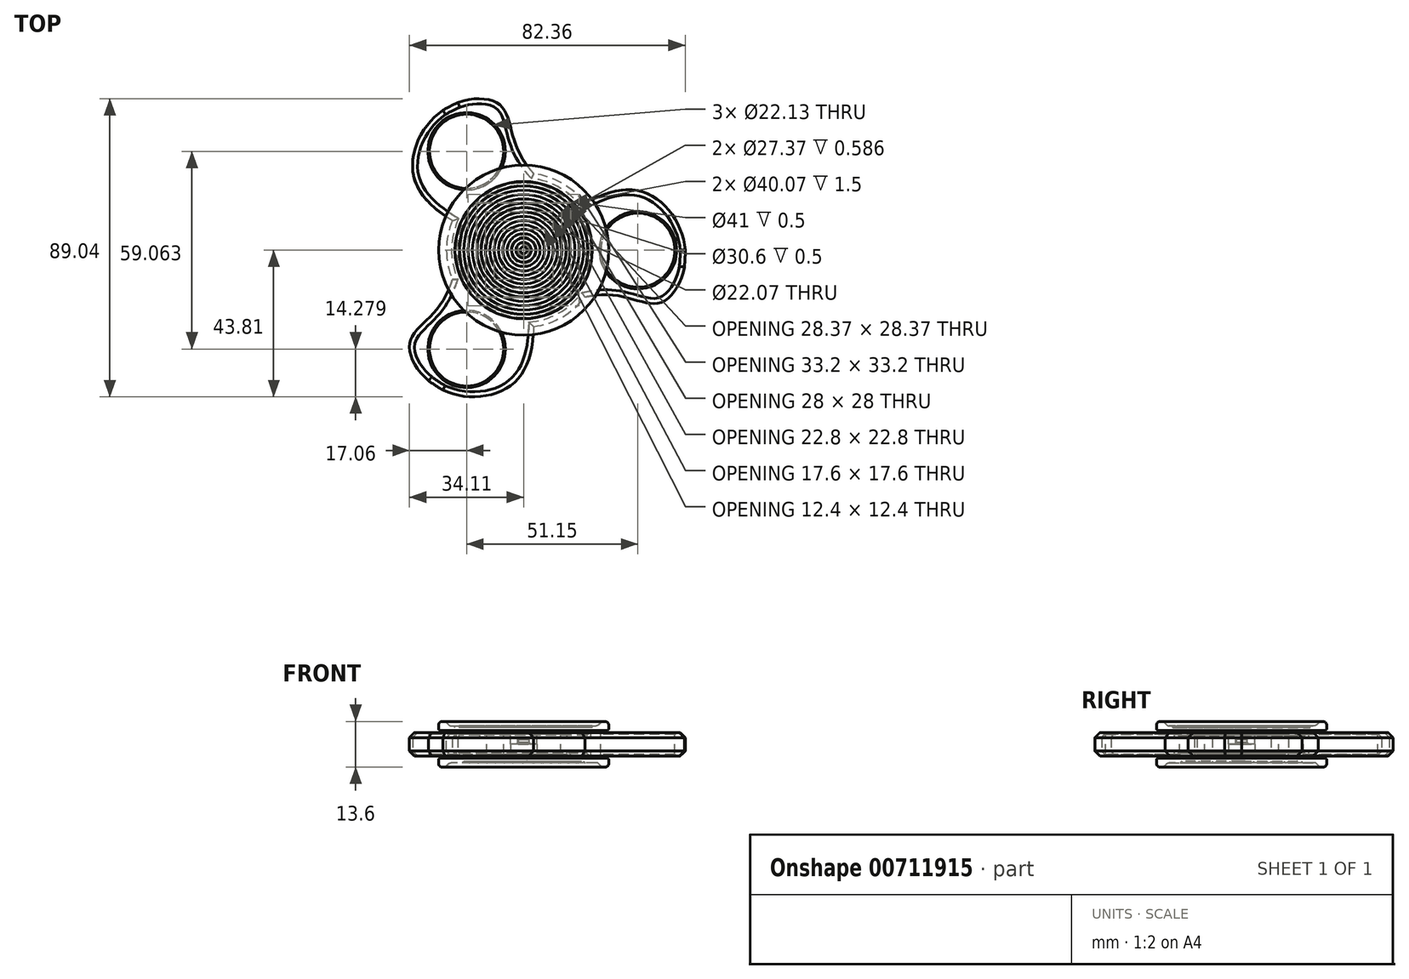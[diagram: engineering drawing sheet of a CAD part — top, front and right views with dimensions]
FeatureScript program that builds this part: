
annotation { "Feature Type Name" : "Feature", "Feature Type Description" : "" }
export const myFeature = defineFeature(function(context is Context, id is Id, definition is map)
    precondition{}
    {
        {
            var Q0;
            Q0=qCreatedBy(makeId("Front.planeOp"),FACE);
            var sketch = newSketch(context, id + "F0", { "sketchPlane" : qUnion([Q0])});
            skLineSegment(sketch, "E0", {"start": v(0, 0) * mm, "end": v(0, 3.5) * mm});
            skLineSegment(sketch, "E1", {"start": v(0, 3.5) * mm, "end": v(13.04, 3.5) * mm});
            skLineSegment(sketch, "E2", {"start": v(13.04, 3.5) * mm, "end": v(13.04, 2) * mm});
            skLineSegment(sketch, "E3", {"start": v(13.04, 2) * mm, "end": v(20.04, 2) * mm});
            skLineSegment(sketch, "E4", {"start": v(20.04, 2) * mm, "end": v(20.04, 3.5) * mm});
            skLineSegment(sketch, "E5", {"start": v(20.04, 3.5) * mm, "end": v(23.04, 3.5) * mm});
            skLineSegment(sketch, "E6", {"start": v(23.04, 3.5) * mm, "end": v(23.04, 0) * mm});
            skLineSegment(sketch, "E7", {"start": v(23.04, 0) * mm, "end": v(45.16, 0) * mm});
            skLineSegment(sketch, "E8", {"start": v(45.16, 0) * mm, "end": v(45.16, 3.5) * mm});
            skLineSegment(sketch, "E9", {"start": v(45.16, 3.5) * mm, "end": v(47.16, 3.5) * mm});
            skLineSegment(sketch, "E10", {"start": v(47.16, 3.5) * mm, "end": v(48.16, 1.5) * mm});
            skLineSegment(sketch, "E11", {"start": v(48.16, 1.5) * mm, "end": v(48.16, 0) * mm});
            skLineSegment(sketch, "E12", {"start": v(48.16, 0) * mm, "end": v(45.16, 0) * mm});
            skLineSegment(sketch, "E13", {"start": v(23.04, 0) * mm, "end": v(11.04, 0) * mm});
            skLineSegment(sketch, "E14", {"start": v(11.04, 0) * mm, "end": v(11.04, 3.5) * mm});
            skLineSegment(sketch, "E15", {"start": v(23.04, 3.5) * mm, "end": v(45.16, 3.5) * mm});
            skLineSegment(sketch, "E16", {"start": v(34.1, 0) * mm, "end": v(34.1, 3.5) * mm});
            skLineSegment(sketch, "E17", {"start": v(13.68, 4.15) * mm, "end": v(13.68, 2.65) * mm});
            skLineSegment(sketch, "E18", {"start": v(13.68, 2.65) * mm, "end": v(19.38, 2.65) * mm});
            skLineSegment(sketch, "E19", {"start": v(19.38, 2.65) * mm, "end": v(19.38, 4.15) * mm});
            skLineSegment(sketch, "E20", {"start": v(19.38, 4.15) * mm, "end": v(25.38, 4.15) * mm});
            skLineSegment(sketch, "E21", {"start": v(25.38, 4.15) * mm, "end": v(25.38, 5.5) * mm});
            skLineSegment(sketch, "E22", {"start": v(25.38, 5.5) * mm, "end": v(0, 5.5) * mm});
            skLineSegment(sketch, "E23", {"start": v(0, 5.5) * mm, "end": v(0, 0) * mm});
            skLineSegment(sketch, "E24", {"start": v(0, 0) * mm, "end": v(3.97, 0) * mm});
            skLineSegment(sketch, "E25", {"start": v(3.97, 0) * mm, "end": v(3.97, 3.5) * mm});
            skLineSegment(sketch, "E26", {"start": v(3.97, 3.5) * mm, "end": v(4.97, 3.5) * mm});
            skLineSegment(sketch, "E27", {"start": v(4.97, 3.5) * mm, "end": v(4.97, 4.15) * mm});
            skLineSegment(sketch, "E28", {"start": v(4.97, 4.15) * mm, "end": v(13.68, 4.15) * mm});
            skLineSegment(sketch, "E29", {"start": v(25.38, 5.5) * mm, "end": v(25.38, 6.8) * mm});
            skLineSegment(sketch, "E30", {"start": v(25.38, 6.8) * mm, "end": v(23.38, 6.8) * mm});
            skLineSegment(sketch, "E31", {"start": v(23.38, 6.8) * mm, "end": v(22.08, 5.5) * mm});
            skLineSegment(sketch, "E32.bottom", {"start": v(1, 5.5) * mm, "end": v(2.3, 5.5) * mm});
            skLineSegment(sketch, "E32.top", {"start": v(1, 5) * mm, "end": v(2.3, 5) * mm});
            skLineSegment(sketch, "E32.left", {"start": v(1, 5.5) * mm, "end": v(1, 5) * mm});
            skLineSegment(sketch, "E32.right", {"start": v(2.3, 5.5) * mm, "end": v(2.3, 5) * mm});
            skLineSegment(sketch, "E33.1.0.0", {"start": v(4.9, 5.5) * mm, "end": v(4.9, 5) * mm});
            skLineSegment(sketch, "E33.1.0.1", {"start": v(3.6, 5) * mm, "end": v(4.9, 5) * mm});
            skLineSegment(sketch, "E33.1.0.2", {"start": v(3.6, 5.5) * mm, "end": v(3.6, 5) * mm});
            skLineSegment(sketch, "E33.2.0.0", {"start": v(7.5, 5.5) * mm, "end": v(7.5, 5) * mm});
            skLineSegment(sketch, "E33.2.0.1", {"start": v(6.2, 5) * mm, "end": v(7.5, 5) * mm});
            skLineSegment(sketch, "E33.2.0.2", {"start": v(6.2, 5.5) * mm, "end": v(6.2, 5) * mm});
            skLineSegment(sketch, "E33.3.0.0", {"start": v(10.1, 5.5) * mm, "end": v(10.1, 5) * mm});
            skLineSegment(sketch, "E33.3.0.1", {"start": v(8.8, 5) * mm, "end": v(10.1, 5) * mm});
            skLineSegment(sketch, "E33.3.0.2", {"start": v(8.8, 5.5) * mm, "end": v(8.8, 5) * mm});
            skLineSegment(sketch, "E33.4.0.0", {"start": v(12.7, 5.5) * mm, "end": v(12.7, 5) * mm});
            skLineSegment(sketch, "E33.4.0.1", {"start": v(11.4, 5) * mm, "end": v(12.7, 5) * mm});
            skLineSegment(sketch, "E33.4.0.2", {"start": v(11.4, 5.5) * mm, "end": v(11.4, 5) * mm});
            skLineSegment(sketch, "E33.5.0.0", {"start": v(15.3, 5.5) * mm, "end": v(15.3, 5) * mm});
            skLineSegment(sketch, "E33.5.0.1", {"start": v(14, 5) * mm, "end": v(15.3, 5) * mm});
            skLineSegment(sketch, "E33.5.0.2", {"start": v(14, 5.5) * mm, "end": v(14, 5) * mm});
            skLineSegment(sketch, "E33.6.0.0", {"start": v(17.9, 5.5) * mm, "end": v(17.9, 5) * mm});
            skLineSegment(sketch, "E33.6.0.1", {"start": v(16.6, 5) * mm, "end": v(17.9, 5) * mm});
            skLineSegment(sketch, "E33.6.0.2", {"start": v(16.6, 5.5) * mm, "end": v(16.6, 5) * mm});
            skLineSegment(sketch, "E33.direction1", {"start": v(2.3, 5) * mm, "end": v(4.9, 5) * mm, "construction": true});
            skLineSegment(sketch, "E34.MirrorCS", {"start": v(2.3, -5.5) * mm, "end": v(2.3, -5) * mm});
            skLineSegment(sketch, "E35.MirrorCS", {"start": v(3.6, -5) * mm, "end": v(4.9, -5) * mm});
            skLineSegment(sketch, "E36.MirrorCS", {"start": v(1, -5.5) * mm, "end": v(2.3, -5.5) * mm});
            skLineSegment(sketch, "E37.MirrorCS", {"start": v(1, -5) * mm, "end": v(2.3, -5) * mm});
            skLineSegment(sketch, "E38.MirrorCS", {"start": v(4.9, -5.5) * mm, "end": v(4.9, -5) * mm});
            skLineSegment(sketch, "E39.MirrorCS", {"start": v(13.04, -3.5) * mm, "end": v(13.04, -2) * mm});
            skLineSegment(sketch, "E40.MirrorCS", {"start": v(6.2, -5.5) * mm, "end": v(6.2, -5) * mm});
            skLineSegment(sketch, "E41.MirrorCS", {"start": v(1, -5.5) * mm, "end": v(1, -5) * mm});
            skLineSegment(sketch, "E42.MirrorCS", {"start": v(3.6, -5.5) * mm, "end": v(3.6, -5) * mm});
            skLineSegment(sketch, "E43.MirrorCS", {"start": v(2.3, -5) * mm, "end": v(4.9, -5) * mm, "construction": true});
            skLineSegment(sketch, "E44.MirrorCS", {"start": v(10.1, -5.5) * mm, "end": v(10.1, -5) * mm});
            skLineSegment(sketch, "E45.MirrorCS", {"start": v(3.97, -3.5) * mm, "end": v(4.97, -3.5) * mm});
            skLineSegment(sketch, "E46.MirrorCS", {"start": v(19.38, -2.65) * mm, "end": v(19.38, -4.15) * mm});
            skLineSegment(sketch, "E47.MirrorCS", {"start": v(17.9, -5.5) * mm, "end": v(17.9, -5) * mm});
            skLineSegment(sketch, "E48.MirrorCS", {"start": v(8.8, -5) * mm, "end": v(10.1, -5) * mm});
            skLineSegment(sketch, "E49.MirrorCS", {"start": v(4.97, -3.5) * mm, "end": v(4.97, -4.15) * mm});
            skLineSegment(sketch, "E50.MirrorCS", {"start": v(19.38, -4.15) * mm, "end": v(25.38, -4.15) * mm});
            skLineSegment(sketch, "E51.MirrorCS", {"start": v(12.7, -5.5) * mm, "end": v(12.7, -5) * mm});
            skLineSegment(sketch, "E52.MirrorCS", {"start": v(16.6, -5) * mm, "end": v(17.9, -5) * mm});
            skLineSegment(sketch, "E53.MirrorCS", {"start": v(25.38, -5.5) * mm, "end": v(25.38, -6.8) * mm});
            skLineSegment(sketch, "E54.MirrorCS", {"start": v(8.8, -5.5) * mm, "end": v(8.8, -5) * mm});
            skLineSegment(sketch, "E55.MirrorCS", {"start": v(11.4, -5) * mm, "end": v(12.7, -5) * mm});
            skLineSegment(sketch, "E56.MirrorCS", {"start": v(16.6, -5.5) * mm, "end": v(16.6, -5) * mm});
            skLineSegment(sketch, "E57.MirrorCS", {"start": v(25.38, -6.8) * mm, "end": v(23.38, -6.8) * mm});
            skLineSegment(sketch, "E58.MirrorCS", {"start": v(14, -5.5) * mm, "end": v(14, -5) * mm});
            skLineSegment(sketch, "E59.MirrorCS", {"start": v(20.04, -3.5) * mm, "end": v(23.04, -3.5) * mm});
            skLineSegment(sketch, "E60.MirrorCS", {"start": v(20.04, -2) * mm, "end": v(20.04, -3.5) * mm});
            skLineSegment(sketch, "E61.MirrorCS", {"start": v(6.2, -5) * mm, "end": v(7.5, -5) * mm});
            skLineSegment(sketch, "E62.MirrorCS", {"start": v(15.3, -5.5) * mm, "end": v(15.3, -5) * mm});
            skLineSegment(sketch, "E63.MirrorCS", {"start": v(47.16, -3.5) * mm, "end": v(48.16, -1.5) * mm});
            skLineSegment(sketch, "E64.MirrorCS", {"start": v(45.16, -3.5) * mm, "end": v(47.16, -3.5) * mm});
            skLineSegment(sketch, "E65.MirrorCS", {"start": v(14, -5) * mm, "end": v(15.3, -5) * mm});
            skLineSegment(sketch, "E66.MirrorCS", {"start": v(7.5, -5.5) * mm, "end": v(7.5, -5) * mm});
            skLineSegment(sketch, "E67.MirrorCS", {"start": v(11.4, -5.5) * mm, "end": v(11.4, -5) * mm});
            skLineSegment(sketch, "E68.MirrorCS", {"start": v(13.69, -4.15) * mm, "end": v(13.69, -2.65) * mm});
            skLineSegment(sketch, "E69.MirrorCS", {"start": v(25.38, -4.15) * mm, "end": v(25.38, -5.5) * mm});
            skLineSegment(sketch, "E70.MirrorCS", {"start": v(23.38, -6.8) * mm, "end": v(22.08, -5.5) * mm});
            skLineSegment(sketch, "E71.MirrorCS", {"start": v(4.97, -4.15) * mm, "end": v(13.68, -4.15) * mm});
            skLineSegment(sketch, "E72.MirrorCS", {"start": v(0, -3.5) * mm, "end": v(13.04, -3.5) * mm});
            skLineSegment(sketch, "E73.MirrorCS", {"start": v(23.04, -3.5) * mm, "end": v(45.16, -3.5) * mm});
            skLineSegment(sketch, "E74.MirrorCS", {"start": v(13.04, -2) * mm, "end": v(20.04, -2) * mm});
            skLineSegment(sketch, "E75.MirrorCS", {"start": v(13.68, -2.65) * mm, "end": v(19.38, -2.65) * mm});
            skLineSegment(sketch, "E76.MirrorCS", {"start": v(25.38, -5.5) * mm, "end": v(0, -5.5) * mm});
            skLineSegment(sketch, "E77.MirrorCS", {"start": v(48.16, -1.5) * mm, "end": v(48.16, 0) * mm});
            skLineSegment(sketch, "E78.MirrorCS", {"start": v(45.16, 0) * mm, "end": v(45.16, -3.5) * mm});
            skLineSegment(sketch, "E79.MirrorCS", {"start": v(34.1, 0) * mm, "end": v(34.1, -3.5) * mm});
            skLineSegment(sketch, "E80.MirrorCS", {"start": v(23.04, -3.5) * mm, "end": v(23.04, 0) * mm});
            skLineSegment(sketch, "E81.MirrorCS", {"start": v(11.04, 0) * mm, "end": v(11.04, -3.5) * mm});
            skLineSegment(sketch, "E82.MirrorCS", {"start": v(3.97, 0) * mm, "end": v(3.97, -3.5) * mm});
            skLineSegment(sketch, "E83.MirrorCS", {"start": v(0, -5.5) * mm, "end": v(0, 0) * mm});
            skLineSegment(sketch, "E84", {"start": v(1.6, 0) * mm, "end": v(1.6, 2) * mm});
            skLineSegment(sketch, "E85", {"start": v(1.6, 2) * mm, "end": v(0, 2) * mm});
            skLineSegment(sketch, "E86.0", {"start": v(1.7, 2.1) * mm, "end": v(0, 2.1) * mm});
            skLineSegment(sketch, "E86.1", {"start": v(1.7, 0) * mm, "end": v(1.7, 2.1) * mm});
            skLineSegment(sketch, "E87.0.7.0", {"start": v(20.5, 5.5) * mm, "end": v(20.5, 5) * mm});
            skLineSegment(sketch, "E87.3.7.0", {"start": v(19.2, 5) * mm, "end": v(20.5, 5) * mm});
            skLineSegment(sketch, "E87.6.7.0", {"start": v(19.2, 5.5) * mm, "end": v(19.2, 5) * mm});
            skSolve(sketch);
        }
        {
            var Q0;
            {var subQ1=sQuery(id+"F0.wireOp",EDGE,"E2");Q0=makeQuery(id+"F0.imprint","IMPRINT",FACE,{"disambiguationData":[TD([[makeQuery(id+"F0.imprint","IMPRINT",EDGE,{"derivedFrom":subQ1}),-1.0]])]});}
            var Q1;
            Q1=makeQuery(id+"F0.imprint","IMPRINT",FACE,{"disambiguationData":[TD([[makeQuery(id+"F0.imprint","IMPRINT",EDGE,{"derivedFrom":sQuery(id+"F0.wireOp",EDGE,"E13")}),1.0]])]});
            var Q2;
            {var subQ0=sQuery(id+"F0.wireOp",EDGE,"E6");Q2=makeQuery(id+"F0.imprint","IMPRINT",FACE,{"disambiguationData":[TD([[makeQuery(id+"F0.imprint","IMPRINT",EDGE,{"derivedFrom":subQ0}),1.0]])]});}
            var Q3;
            {var subQ2=sQuery(id+"F0.wireOp",EDGE,"E79.MirrorCS");Q3=makeQuery(id+"F0.imprint","IMPRINT",FACE,{"disambiguationData":[TD([[makeQuery(id+"F0.imprint","IMPRINT",EDGE,{"derivedFrom":subQ2}),-1.0]])]});}
            var Q4;
            {var subQ0=sQuery(id+"F0.wireOp",EDGE,"E8");Q4=makeQuery(id+"F0.imprint","IMPRINT",FACE,{"disambiguationData":[TD([[makeQuery(id+"F0.imprint","IMPRINT",EDGE,{"derivedFrom":subQ0}),1.0]])]});}
            var Q5;
            {var subQ0=sQuery(id+"F0.wireOp",EDGE,"E78.MirrorCS");Q5=makeQuery(id+"F0.imprint","IMPRINT",FACE,{"disambiguationData":[TD([[makeQuery(id+"F0.imprint","IMPRINT",EDGE,{"derivedFrom":subQ0}),-1.0]])]});}
            var Q6;
            Q6=makeQuery(id+"F0.imprint","IMPRINT",FACE,{"disambiguationData":[TD([[makeQuery(id+"F0.imprint","IMPRINT",EDGE,{"derivedFrom":sQuery(id+"F0.wireOp",EDGE,"E8")}),-1.0]])]});
            var Q7;
            Q7=makeQuery(id+"F0.imprint","IMPRINT",FACE,{"disambiguationData":[TD([[makeQuery(id+"F0.imprint","IMPRINT",EDGE,{"derivedFrom":sQuery(id+"F0.wireOp",EDGE,"E12")}),1.0]])]});
            var Q8;
            Q8=sQuery(id+"F0.wireOp",EDGE,"E23");
            revolve(context, id + "F1", {"surfaceOperationType" : NewSurfaceOperationType.NEW, "entities" : qUnion([Q0, Q1, Q2, Q3, Q4, Q5, Q6, Q7]), "axis" : qUnion([Q8]), "revolveType" : RevolveType.FULL});
        }
        {
            var Q0;
            {var subQ0=sQuery(id+"F0.wireOp",EDGE,"E8");Q0=makeQuery(id+"F0.imprint","IMPRINT",FACE,{"disambiguationData":[TD([[makeQuery(id+"F0.imprint","IMPRINT",EDGE,{"derivedFrom":subQ0}),1.0]])]});}
            var Q1;
            {var subQ0=sQuery(id+"F0.wireOp",EDGE,"E78.MirrorCS");Q1=makeQuery(id+"F0.imprint","IMPRINT",FACE,{"disambiguationData":[TD([[makeQuery(id+"F0.imprint","IMPRINT",EDGE,{"derivedFrom":subQ0}),-1.0]])]});}
            var Q2;
            Q2=sQuery(id+"F0.wireOp",EDGE,"E79.MirrorCS");
            revolve(context, id + "F2", {"surfaceOperationType" : NewSurfaceOperationType.NEW, "entities" : qUnion([Q0, Q1]), "axis" : qUnion([Q2]), "revolveType" : RevolveType.FULL});
        }
        {
            var Q0;
            Q0=makeQuery(id+"F0.imprint","IMPRINT",FACE,{"disambiguationData":[TD([[makeQuery(id+"F0.imprint","IMPRINT",EDGE,{"derivedFrom":sQuery(id+"F0.wireOp",EDGE,"E17")}),1.0]])]});
            var Q1;
            {var subQ0=sQuery(id+"F0.wireOp",EDGE,"E29");Q1=makeQuery(id+"F0.imprint","IMPRINT",FACE,{"disambiguationData":[TD([[makeQuery(id+"F0.imprint","IMPRINT",EDGE,{"derivedFrom":subQ0}),1.0]])]});}
            var Q2;
            {var subQ0=sQuery(id+"F0.wireOp",EDGE,"E25");Q2=makeQuery(id+"F0.imprint","IMPRINT",FACE,{"disambiguationData":[TD([[makeQuery(id+"F0.imprint","IMPRINT",EDGE,{"derivedFrom":subQ0}),1.0]])]});}
            var Q3;
            Q3=sQuery(id+"F0.wireOp",EDGE,"E23");
            revolve(context, id + "F3", {"surfaceOperationType" : NewSurfaceOperationType.NEW, "entities" : qUnion([Q0, Q1, Q2]), "axis" : qUnion([Q3]), "revolveType" : RevolveType.FULL});
        }
        {
            var Q0;
            {var subQ15=sQuery(id+"F0.wireOp",EDGE,"E34.MirrorCS");Q0=makeQuery(id+"F0.imprint","IMPRINT",FACE,{"disambiguationData":[TD([[makeQuery(id+"F0.imprint","IMPRINT",EDGE,{"derivedFrom":subQ15}),-1.0]])]});}
            var Q1;
            {var subQ3=sQuery(id+"F0.wireOp",EDGE,"E82.MirrorCS");Q1=makeQuery(id+"F0.imprint","IMPRINT",FACE,{"disambiguationData":[TD([[makeQuery(id+"F0.imprint","IMPRINT",EDGE,{"derivedFrom":subQ3}),-1.0]])]});}
            var Q2;
            {var subQ4=sQuery(id+"F0.wireOp",EDGE,"E84");Q2=makeQuery(id+"F0.imprint","IMPRINT",FACE,{"disambiguationData":[TD([[makeQuery(id+"F0.imprint","IMPRINT",EDGE,{"derivedFrom":subQ4}),1.0]])]});}
            var Q3;
            {var subQ0=sQuery(id+"F0.wireOp",EDGE,"E53.MirrorCS");Q3=makeQuery(id+"F0.imprint","IMPRINT",FACE,{"disambiguationData":[TD([[makeQuery(id+"F0.imprint","IMPRINT",EDGE,{"derivedFrom":subQ0}),-1.0]])]});}
            var Q4;
            Q4=sQuery(id+"F0.wireOp",EDGE,"E83.MirrorCS");
            revolve(context, id + "F4", {"surfaceOperationType" : NewSurfaceOperationType.NEW, "entities" : qUnion([Q0, Q1, Q2, Q3]), "axis" : qUnion([Q4]), "revolveType" : RevolveType.FULL});
        }
        {
            var Q0;
            Q0=makeQuery(id+"F2.opRevolve","SWEPT_BODY",BODY,{"disambiguationData":[OSD([sQuery(id+"F0.wireOp",EDGE,"E8"),sQuery(id+"F0.wireOp",EDGE,"E15"),sQuery(id+"F0.wireOp",EDGE,"E16"),sQuery(id+"F0.wireOp",EDGE,"E73.MirrorCS"),sQuery(id+"F0.wireOp",EDGE,"E78.MirrorCS"),sQuery(id+"F0.wireOp",EDGE,"E79.MirrorCS")])]});
            var Q1;
            Q1=makeQuery(id+"F1.opRevolve","SWEPT_EDGE",EDGE,{"disambiguationData":[OSD([sQuery(id+"F0.wireOp",EDGE,"E72.MirrorCS"),sQuery(id+"F0.wireOp",EDGE,"E81.MirrorCS")])]});
            circularPattern(context, id + "F5", {"entities" : qUnion([Q0]), "axis" : qUnion([Q1]), "angle" : 360 * degree, "instanceCount" : 3, "equalSpace" : true});
        }
        {
            var Q0;
            Q0=qCreatedBy(makeId("Top.planeOp"),FACE);
            var sketch = newSketch(context, id + "F6", { "sketchPlane" : qUnion([Q0])});
            skCircle(sketch, "E88", {"center": v(0, 0) * mm, "radius": 48.25 * mm});
            skFitSpline(sketch, "E89", {"points": [v(0, -25) * mm, v(27.25, -13.5) * mm, v(41.25, -15.5) * mm, v(48.25, 0) * mm, v(34, 17.78) * mm, v(0, 0) * mm], "startDerivative": vector(107.2, 120.6) * mm, "endDerivative": vector(-125.88, -120.18) * mm});
            skCircle(sketch, "E90", {"center": v(0, 0) * mm, "radius": 22.05 * mm});
            skSolve(sketch);
        }
        {
            var Q0;
            {var subQ0=sQuery(id+"F6.wireOp",EDGE,"E89");var subQ1=sQuery(id+"F6.wireOp",EDGE,"E88");var subQ2=makeQuery(id+"F6.imprint","INTERSECT",VERTEX,{"disambiguationData":[OD(0.0)],"derivedFrom":[subQ1,subQ0]});Q0=makeQuery(id+"F6.imprint","IMPRINT",FACE,{"disambiguationData":[TD([[makeQuery(id+"F6.imprint","IMPRINT",EDGE,{"disambiguationData":[TD([[subQ2,-1.0]])],"derivedFrom":subQ1}),1.0]])]});}
            extrude(context, id + "F7", {"entities" : qUnion([Q0]), "depth" : 3.5 * mm, "offsetDistance" : 25 * mm, "hasSecondDirection" : true, "secondDirectionOppositeDirection" : true, "secondDirectionDepth" : 3.5 * mm});
        }
        {
            var Q0;
            Q0=makeQuery(id+"F7.opExtrude","SWEPT_BODY",BODY,{"disambiguationData":[OSD([sQuery(id+"F6.wireOp",EDGE,"E88"),sQuery(id+"F6.wireOp",EDGE,"E89"),sQuery(id+"F6.wireOp",EDGE,"E90")])]});
            var Q1;
            Q1=makeQuery(id+"F1.opRevolve","SWEPT_FACE",FACE,{"disambiguationData":[OSD([sQuery(id+"F0.wireOp",EDGE,"E14"),sQuery(id+"F0.wireOp",EDGE,"E81.MirrorCS")])]});
            circularPattern(context, id + "F8", {"entities" : qUnion([Q0]), "axis" : qUnion([Q1]), "angle" : 360 * degree, "instanceCount" : 3, "equalSpace" : true});
        }
        {
            var Q0;
            {var subQ1=sQuery(id+"F0.wireOp",EDGE,"E2");Q0=makeQuery(id+"F0.imprint","IMPRINT",FACE,{"disambiguationData":[TD([[makeQuery(id+"F0.imprint","IMPRINT",EDGE,{"derivedFrom":subQ1}),-1.0]])]});}
            var Q1;
            Q1=makeQuery(id+"F0.imprint","IMPRINT",FACE,{"disambiguationData":[TD([[makeQuery(id+"F0.imprint","IMPRINT",EDGE,{"derivedFrom":sQuery(id+"F0.wireOp",EDGE,"E13")}),1.0]])]});
            var Q2;
            Q2=sQuery(id+"F0.wireOp",EDGE,"E23");
            revolve(context, id + "F9", {"surfaceOperationType" : NewSurfaceOperationType.NEW, "entities" : qUnion([Q0, Q1]), "axis" : qUnion([Q2]), "revolveType" : RevolveType.FULL});
        }
        {
            var Q0;
            Q0=makeQuery(id+"F8.opPattern","COPY",BODY,{"derivedFrom":makeQuery(id+"F7.opExtrude","SWEPT_BODY",BODY,{"disambiguationData":[OSD([sQuery(id+"F6.wireOp",EDGE,"E88"),sQuery(id+"F6.wireOp",EDGE,"E89"),sQuery(id+"F6.wireOp",EDGE,"E90")])]}),"instanceName":"2"});
            var Q1;
            Q1=makeQuery(id+"F8.opPattern","COPY",BODY,{"derivedFrom":makeQuery(id+"F7.opExtrude","SWEPT_BODY",BODY,{"disambiguationData":[OSD([sQuery(id+"F6.wireOp",EDGE,"E88"),sQuery(id+"F6.wireOp",EDGE,"E89"),sQuery(id+"F6.wireOp",EDGE,"E90")])]}),"instanceName":"1"});
            var Q2;
            Q2=makeQuery(id+"F7.opExtrude","SWEPT_BODY",BODY,{"disambiguationData":[OSD([sQuery(id+"F6.wireOp",EDGE,"E88"),sQuery(id+"F6.wireOp",EDGE,"E89"),sQuery(id+"F6.wireOp",EDGE,"E90")])]});
            var Q3;
            Q3=makeQuery(id+"F9.opRevolve","SWEPT_BODY",BODY,{"disambiguationData":[OSD([sQuery(id+"F0.wireOp",EDGE,"E1"),sQuery(id+"F0.wireOp",EDGE,"E2"),sQuery(id+"F0.wireOp",EDGE,"E3"),sQuery(id+"F0.wireOp",EDGE,"E4"),sQuery(id+"F0.wireOp",EDGE,"E5"),sQuery(id+"F0.wireOp",EDGE,"E6"),sQuery(id+"F0.wireOp",EDGE,"E23"),sQuery(id+"F0.wireOp",EDGE,"E26"),sQuery(id+"F0.wireOp",EDGE,"E39.MirrorCS"),sQuery(id+"F0.wireOp",EDGE,"E59.MirrorCS"),sQuery(id+"F0.wireOp",EDGE,"E60.MirrorCS"),sQuery(id+"F0.wireOp",EDGE,"E72.MirrorCS"),sQuery(id+"F0.wireOp",EDGE,"E74.MirrorCS"),sQuery(id+"F0.wireOp",EDGE,"E80.MirrorCS"),sQuery(id+"F0.wireOp",EDGE,"E83.MirrorCS")])]});
            booleanBodies(context, id + "F10", {"operationType" : BooleanOperationType.UNION, "tools" : qUnion([Q0, Q1, Q2, Q3])});
        }
        {
            var Q0;
            Q0=makeQuery(id+"F1.opRevolve","SWEPT_BODY",BODY,{"disambiguationData":[OSD([sQuery(id+"F0.wireOp",EDGE,"E1"),sQuery(id+"F0.wireOp",EDGE,"E2"),sQuery(id+"F0.wireOp",EDGE,"E3"),sQuery(id+"F0.wireOp",EDGE,"E4"),sQuery(id+"F0.wireOp",EDGE,"E5"),sQuery(id+"F0.wireOp",EDGE,"E9"),sQuery(id+"F0.wireOp",EDGE,"E10"),sQuery(id+"F0.wireOp",EDGE,"E11"),sQuery(id+"F0.wireOp",EDGE,"E14"),sQuery(id+"F0.wireOp",EDGE,"E15"),sQuery(id+"F0.wireOp",EDGE,"E39.MirrorCS"),sQuery(id+"F0.wireOp",EDGE,"E59.MirrorCS"),sQuery(id+"F0.wireOp",EDGE,"E60.MirrorCS"),sQuery(id+"F0.wireOp",EDGE,"E63.MirrorCS"),sQuery(id+"F0.wireOp",EDGE,"E64.MirrorCS"),sQuery(id+"F0.wireOp",EDGE,"E72.MirrorCS"),sQuery(id+"F0.wireOp",EDGE,"E73.MirrorCS"),sQuery(id+"F0.wireOp",EDGE,"E74.MirrorCS"),sQuery(id+"F0.wireOp",EDGE,"E77.MirrorCS"),sQuery(id+"F0.wireOp",EDGE,"E81.MirrorCS")])]});
            deleteBodies(context, id + "F11", {"entities" : qUnion([Q0])});
        }
        {
            var Q0;
            Q0=makeQuery(id+"F5.opPattern","COPY",BODY,{"derivedFrom":makeQuery(id+"F2.opRevolve","SWEPT_BODY",BODY,{"disambiguationData":[OSD([sQuery(id+"F0.wireOp",EDGE,"E8"),sQuery(id+"F0.wireOp",EDGE,"E15"),sQuery(id+"F0.wireOp",EDGE,"E16"),sQuery(id+"F0.wireOp",EDGE,"E73.MirrorCS"),sQuery(id+"F0.wireOp",EDGE,"E78.MirrorCS"),sQuery(id+"F0.wireOp",EDGE,"E79.MirrorCS")])]}),"instanceName":"2"});
            var Q1;
            Q1=makeQuery(id+"F5.opPattern","COPY",BODY,{"derivedFrom":makeQuery(id+"F2.opRevolve","SWEPT_BODY",BODY,{"disambiguationData":[OSD([sQuery(id+"F0.wireOp",EDGE,"E8"),sQuery(id+"F0.wireOp",EDGE,"E15"),sQuery(id+"F0.wireOp",EDGE,"E16"),sQuery(id+"F0.wireOp",EDGE,"E73.MirrorCS"),sQuery(id+"F0.wireOp",EDGE,"E78.MirrorCS"),sQuery(id+"F0.wireOp",EDGE,"E79.MirrorCS")])]}),"instanceName":"1"});
            var Q2;
            Q2=makeQuery(id+"F2.opRevolve","SWEPT_BODY",BODY,{"disambiguationData":[OSD([sQuery(id+"F0.wireOp",EDGE,"E8"),sQuery(id+"F0.wireOp",EDGE,"E15"),sQuery(id+"F0.wireOp",EDGE,"E16"),sQuery(id+"F0.wireOp",EDGE,"E73.MirrorCS"),sQuery(id+"F0.wireOp",EDGE,"E78.MirrorCS"),sQuery(id+"F0.wireOp",EDGE,"E79.MirrorCS")])]});
            var Q3;
            Q3=makeQuery(id+"F8.opPattern","COPY",BODY,{"derivedFrom":makeQuery(id+"F7.opExtrude","SWEPT_BODY",BODY,{"disambiguationData":[OSD([sQuery(id+"F6.wireOp",EDGE,"E88"),sQuery(id+"F6.wireOp",EDGE,"E89"),sQuery(id+"F6.wireOp",EDGE,"E90")])]}),"instanceName":"2"});
            booleanBodies(context, id + "F12", {"operationType" : BooleanOperationType.SUBTRACTION, "tools" : qUnion([Q0, Q1, Q2]), "targets" : qUnion([Q3])});
        }
        {
            var Q0;
            Q0=makeQuery(id+"F9.opRevolve","SWEPT_EDGE",EDGE,{"disambiguationData":[OSD([sQuery(id+"F0.wireOp",EDGE,"E39.MirrorCS"),sQuery(id+"F0.wireOp",EDGE,"E72.MirrorCS")])]});
            var Q1;
            Q1=makeQuery(id+"F9.opRevolve","SWEPT_EDGE",EDGE,{"disambiguationData":[OSD([sQuery(id+"F0.wireOp",EDGE,"E72.MirrorCS"),sQuery(id+"F0.wireOp",EDGE,"E81.MirrorCS")])]});
            var Q2;
            Q2=makeQuery(id+"F12.opBoolean","COPY",FACE,{"derivedFrom":makeQuery(id+"F5.opPattern","COPY",FACE,{"derivedFrom":makeQuery(id+"F2.opRevolve","SWEPT_FACE",FACE,{"disambiguationData":[OSD([sQuery(id+"F0.wireOp",EDGE,"E8"),sQuery(id+"F0.wireOp",EDGE,"E78.MirrorCS")])]}),"instanceName":"1"})});
            var Q3;
            Q3=makeQuery(id+"F12.opBoolean","COPY",FACE,{"derivedFrom":makeQuery(id+"F5.opPattern","COPY",FACE,{"derivedFrom":makeQuery(id+"F2.opRevolve","SWEPT_FACE",FACE,{"disambiguationData":[OSD([sQuery(id+"F0.wireOp",EDGE,"E8"),sQuery(id+"F0.wireOp",EDGE,"E78.MirrorCS")])]}),"instanceName":"2"})});
            var Q4;
            Q4=makeQuery(id+"F12.opBoolean","COPY",FACE,{"derivedFrom":makeQuery(id+"F2.opRevolve","SWEPT_FACE",FACE,{"disambiguationData":[OSD([sQuery(id+"F0.wireOp",EDGE,"E8"),sQuery(id+"F0.wireOp",EDGE,"E78.MirrorCS")])]})});
            var Q5;
            Q5=makeQuery(id+"F9.opRevolve","SWEPT_FACE",FACE,{"disambiguationData":[OSD([sQuery(id+"F0.wireOp",EDGE,"E1")])]});
            var Q6;
            Q6=makeQuery(id+"F4.opRevolve","SWEPT_EDGE",EDGE,{"disambiguationData":[OSD([sQuery(id+"F0.wireOp",EDGE,"E84"),sQuery(id+"F0.wireOp",EDGE,"E85")])]});
            var Q7;
            Q7=makeQuery(id+"F4.opRevolve","SWEPT_EDGE",EDGE,{"disambiguationData":[OSD([sQuery(id+"F0.wireOp",EDGE,"E68.MirrorCS"),sQuery(id+"F0.wireOp",EDGE,"E75.MirrorCS")])]});
            var Q8;
            Q8=makeQuery(id+"F4.opRevolve","SWEPT_EDGE",EDGE,{"disambiguationData":[OSD([sQuery(id+"F0.wireOp",EDGE,"E46.MirrorCS"),sQuery(id+"F0.wireOp",EDGE,"E75.MirrorCS")])]});
            var Q9;
            Q9=makeQuery(id+"F3.opRevolve","SWEPT_EDGE",EDGE,{"disambiguationData":[OSD([sQuery(id+"F0.wireOp",EDGE,"E24"),sQuery(id+"F0.wireOp",EDGE,"E86.1")])]});
            var Q10;
            Q10=makeQuery(id+"F3.opRevolve","SWEPT_EDGE",EDGE,{"disambiguationData":[OSD([sQuery(id+"F0.wireOp",EDGE,"E17"),sQuery(id+"F0.wireOp",EDGE,"E18")])]});
            var Q11;
            Q11=makeQuery(id+"F3.opRevolve","SWEPT_EDGE",EDGE,{"disambiguationData":[OSD([sQuery(id+"F0.wireOp",EDGE,"E18"),sQuery(id+"F0.wireOp",EDGE,"E19")])]});
            chamfer(context, id + "F13", {"entities" : qUnion([Q0, Q1, Q2, Q3, Q4, Q5, Q6, Q7, Q8, Q9, Q10, Q11]), "width" : 0.5 * mm, "tangentPropagation" : true});
        }
        {
            var Q0;
            Q0=makeQuery(id+"F3.opRevolve","SWEPT_EDGE",EDGE,{"disambiguationData":[OSD([sQuery(id+"F0.wireOp",EDGE,"E30"),sQuery(id+"F0.wireOp",EDGE,"E31")])]});
            var Q1;
            Q1=makeQuery(id+"F3.opRevolve","SWEPT_EDGE",EDGE,{"disambiguationData":[OSD([sQuery(id+"F0.wireOp",EDGE,"E29"),sQuery(id+"F0.wireOp",EDGE,"E30")])]});
            var Q2;
            Q2=makeQuery(id+"F4.opRevolve","SWEPT_EDGE",EDGE,{"disambiguationData":[OSD([sQuery(id+"F0.wireOp",EDGE,"E53.MirrorCS"),sQuery(id+"F0.wireOp",EDGE,"E57.MirrorCS")])]});
            var Q3;
            Q3=makeQuery(id+"F4.opRevolve","SWEPT_EDGE",EDGE,{"disambiguationData":[OSD([sQuery(id+"F0.wireOp",EDGE,"E57.MirrorCS"),sQuery(id+"F0.wireOp",EDGE,"E70.MirrorCS")])]});
            var Q4;
            Q4=makeQuery(id+"F4.opRevolve","SWEPT_EDGE",EDGE,{"disambiguationData":[OSD([sQuery(id+"F0.wireOp",EDGE,"E41.MirrorCS"),sQuery(id+"F0.wireOp",EDGE,"E76.MirrorCS")])]});
            var Q5;
            Q5=makeQuery(id+"F3.opRevolve","SWEPT_EDGE",EDGE,{"disambiguationData":[OSD([sQuery(id+"F0.wireOp",EDGE,"E22"),sQuery(id+"F0.wireOp",EDGE,"E32.bottom"),sQuery(id+"F0.wireOp",EDGE,"E32.left")])]});
            var Q6;
            Q6=makeQuery(id+"F3.opRevolve","SWEPT_EDGE",EDGE,{"disambiguationData":[OSD([sQuery(id+"F0.wireOp",EDGE,"E22"),sQuery(id+"F0.wireOp",EDGE,"E31")])]});
            var Q7;
            Q7=makeQuery(id+"F4.opRevolve","SWEPT_EDGE",EDGE,{"disambiguationData":[OSD([sQuery(id+"F0.wireOp",EDGE,"E70.MirrorCS"),sQuery(id+"F0.wireOp",EDGE,"E76.MirrorCS")])]});
            var Q8;
            {var subQ0=sQuery(id+"F0.wireOp",EDGE,"E19");Q8=makeQuery(id+"F13.opChamfer","BLEND_EDGE",EDGE,{"blendedFrom":[makeQuery(id+"F3.opRevolve","SWEPT_EDGE",EDGE,{"disambiguationData":[OSD([sQuery(id+"F0.wireOp",EDGE,"E18"),subQ0])]}),makeQuery(id+"F3.opRevolve","SWEPT_FACE",FACE,{"disambiguationData":[OSD([subQ0])]})],"blendedInto":[makeQuery(id+"F3.opRevolve","SWEPT_FACE",FACE,{"disambiguationData":[OSD([subQ0])]})]});}
            var Q9;
            {var subQ0=sQuery(id+"F0.wireOp",EDGE,"E17");Q9=makeQuery(id+"F13.opChamfer","BLEND_EDGE",EDGE,{"blendedFrom":[makeQuery(id+"F3.opRevolve","SWEPT_EDGE",EDGE,{"disambiguationData":[OSD([subQ0,sQuery(id+"F0.wireOp",EDGE,"E18")])]}),makeQuery(id+"F3.opRevolve","SWEPT_FACE",FACE,{"disambiguationData":[OSD([subQ0])]})],"blendedInto":[makeQuery(id+"F3.opRevolve","SWEPT_FACE",FACE,{"disambiguationData":[OSD([subQ0])]})]});}
            var Q10;
            {var subQ0=sQuery(id+"F0.wireOp",EDGE,"E68.MirrorCS");Q10=makeQuery(id+"F13.opChamfer","BLEND_EDGE",EDGE,{"blendedFrom":[makeQuery(id+"F4.opRevolve","SWEPT_EDGE",EDGE,{"disambiguationData":[OSD([subQ0,sQuery(id+"F0.wireOp",EDGE,"E75.MirrorCS")])]}),makeQuery(id+"F4.opRevolve","SWEPT_FACE",FACE,{"disambiguationData":[OSD([subQ0])]})],"blendedInto":[makeQuery(id+"F4.opRevolve","SWEPT_FACE",FACE,{"disambiguationData":[OSD([subQ0])]})]});}
            var Q11;
            {var subQ0=sQuery(id+"F0.wireOp",EDGE,"E46.MirrorCS");Q11=makeQuery(id+"F13.opChamfer","BLEND_EDGE",EDGE,{"blendedFrom":[makeQuery(id+"F4.opRevolve","SWEPT_EDGE",EDGE,{"disambiguationData":[OSD([subQ0,sQuery(id+"F0.wireOp",EDGE,"E75.MirrorCS")])]}),makeQuery(id+"F4.opRevolve","SWEPT_FACE",FACE,{"disambiguationData":[OSD([subQ0])]})],"blendedInto":[makeQuery(id+"F4.opRevolve","SWEPT_FACE",FACE,{"disambiguationData":[OSD([subQ0])]})]});}
            fillet(context, id + "F14", {"entities" : qUnion([Q0, Q1, Q2, Q3, Q4, Q5, Q6, Q7, Q8, Q9, Q10, Q11]), "radius" : 1 * mm, "tangentPropagation" : true, "allowEdgeOverflow" : false});
        }
        {
            var Q0;
            {var subQ0=sQuery(id+"F0.wireOp",EDGE,"E22");Q0=makeQuery(id+"F3.opRevolve","SWEPT_FACE",FACE,{"disambiguationData":[OSD([subQ0]),TDD([makeQuery(id+"F0.imprint","IMPRINT",EDGE,{"disambiguationData":[TD([[makeQuery(id+"F0.imprint","INTERSECT",VERTEX,{"derivedFrom":[subQ0,sQuery(id+"F0.wireOp",EDGE,"E33.1.0.2")]}),-1.0]])],"derivedFrom":subQ0})])]});}
            var Q1;
            {var subQ0=sQuery(id+"F0.wireOp",EDGE,"E22");Q1=makeQuery(id+"F3.opRevolve","SWEPT_FACE",FACE,{"disambiguationData":[OSD([subQ0]),TDD([makeQuery(id+"F0.imprint","IMPRINT",EDGE,{"disambiguationData":[TD([[makeQuery(id+"F0.imprint","INTERSECT",VERTEX,{"derivedFrom":[subQ0,sQuery(id+"F0.wireOp",EDGE,"E33.1.0.0")]}),1.0]])],"derivedFrom":subQ0})])]});}
            var Q2;
            {var subQ0=sQuery(id+"F0.wireOp",EDGE,"E22");Q2=makeQuery(id+"F3.opRevolve","SWEPT_FACE",FACE,{"disambiguationData":[OSD([subQ0]),TDD([makeQuery(id+"F0.imprint","IMPRINT",EDGE,{"disambiguationData":[TD([[makeQuery(id+"F0.imprint","INTERSECT",VERTEX,{"derivedFrom":[subQ0,sQuery(id+"F0.wireOp",EDGE,"E33.2.0.0")]}),1.0]])],"derivedFrom":subQ0})])]});}
            var Q3;
            {var subQ0=sQuery(id+"F0.wireOp",EDGE,"E22");Q3=makeQuery(id+"F3.opRevolve","SWEPT_FACE",FACE,{"disambiguationData":[OSD([subQ0]),TDD([makeQuery(id+"F0.imprint","IMPRINT",EDGE,{"disambiguationData":[TD([[makeQuery(id+"F0.imprint","INTERSECT",VERTEX,{"derivedFrom":[subQ0,sQuery(id+"F0.wireOp",EDGE,"E33.3.0.0")]}),1.0]])],"derivedFrom":subQ0})])]});}
            var Q4;
            {var subQ0=sQuery(id+"F0.wireOp",EDGE,"E22");Q4=makeQuery(id+"F3.opRevolve","SWEPT_FACE",FACE,{"disambiguationData":[OSD([subQ0]),TDD([makeQuery(id+"F0.imprint","IMPRINT",EDGE,{"disambiguationData":[TD([[makeQuery(id+"F0.imprint","INTERSECT",VERTEX,{"derivedFrom":[subQ0,sQuery(id+"F0.wireOp",EDGE,"E33.4.0.0")]}),1.0]])],"derivedFrom":subQ0})])]});}
            var Q5;
            Q5=makeQuery(id+"F3.opRevolve","SWEPT_EDGE",EDGE,{"disambiguationData":[OSD([sQuery(id+"F0.wireOp",EDGE,"E22"),sQuery(id+"F0.wireOp",EDGE,"E33.6.0.2")])]});
            var Q6;
            Q6=makeQuery(id+"F3.opRevolve","SWEPT_EDGE",EDGE,{"disambiguationData":[OSD([sQuery(id+"F0.wireOp",EDGE,"E22"),sQuery(id+"F0.wireOp",EDGE,"E33.6.0.0")])]});
            var Q7;
            {var subQ0=sQuery(id+"F0.wireOp",EDGE,"E76.MirrorCS");Q7=makeQuery(id+"F4.opRevolve","SWEPT_FACE",FACE,{"disambiguationData":[OSD([subQ0]),TDD([makeQuery(id+"F0.imprint","IMPRINT",EDGE,{"disambiguationData":[TD([[makeQuery(id+"F0.imprint","INTERSECT",VERTEX,{"derivedFrom":[sQuery(id+"F0.wireOp",EDGE,"E34.MirrorCS"),subQ0]}),1.0]])],"derivedFrom":subQ0})])]});}
            var Q8;
            {var subQ0=sQuery(id+"F0.wireOp",EDGE,"E76.MirrorCS");Q8=makeQuery(id+"F4.opRevolve","SWEPT_FACE",FACE,{"disambiguationData":[OSD([subQ0]),TDD([makeQuery(id+"F0.imprint","IMPRINT",EDGE,{"disambiguationData":[TD([[makeQuery(id+"F0.imprint","INTERSECT",VERTEX,{"derivedFrom":[sQuery(id+"F0.wireOp",EDGE,"E38.MirrorCS"),subQ0]}),1.0]])],"derivedFrom":subQ0})])]});}
            var Q9;
            Q9=makeQuery(id+"F4.opRevolve","SWEPT_EDGE",EDGE,{"disambiguationData":[OSD([sQuery(id+"F0.wireOp",EDGE,"E54.MirrorCS"),sQuery(id+"F0.wireOp",EDGE,"E76.MirrorCS")])]});
            var Q10;
            {var subQ0=sQuery(id+"F0.wireOp",EDGE,"E76.MirrorCS");Q10=makeQuery(id+"F4.opRevolve","SWEPT_FACE",FACE,{"disambiguationData":[OSD([subQ0]),TDD([makeQuery(id+"F0.imprint","IMPRINT",EDGE,{"disambiguationData":[TD([[makeQuery(id+"F0.imprint","INTERSECT",VERTEX,{"derivedFrom":[sQuery(id+"F0.wireOp",EDGE,"E56.MirrorCS"),subQ0]}),-1.0]])],"derivedFrom":subQ0})])]});}
            var Q11;
            {var subQ0=sQuery(id+"F0.wireOp",EDGE,"E76.MirrorCS");Q11=makeQuery(id+"F4.opRevolve","SWEPT_FACE",FACE,{"disambiguationData":[OSD([subQ0]),TDD([makeQuery(id+"F0.imprint","IMPRINT",EDGE,{"disambiguationData":[TD([[makeQuery(id+"F0.imprint","INTERSECT",VERTEX,{"derivedFrom":[sQuery(id+"F0.wireOp",EDGE,"E51.MirrorCS"),subQ0]}),1.0]])],"derivedFrom":subQ0})])]});}
            var Q12;
            {var subQ0=sQuery(id+"F0.wireOp",EDGE,"E76.MirrorCS");Q12=makeQuery(id+"F4.opRevolve","SWEPT_FACE",FACE,{"disambiguationData":[OSD([subQ0]),TDD([makeQuery(id+"F0.imprint","IMPRINT",EDGE,{"disambiguationData":[TD([[makeQuery(id+"F0.imprint","INTERSECT",VERTEX,{"derivedFrom":[sQuery(id+"F0.wireOp",EDGE,"E44.MirrorCS"),subQ0]}),1.0]])],"derivedFrom":subQ0})])]});}
            var Q13;
            Q13=makeQuery(id+"F4.opRevolve","SWEPT_EDGE",EDGE,{"disambiguationData":[OSD([sQuery(id+"F0.wireOp",EDGE,"E66.MirrorCS"),sQuery(id+"F0.wireOp",EDGE,"E76.MirrorCS")])]});
            var Q14;
            Q14=makeQuery(id+"F4.opRevolve","SWEPT_EDGE",EDGE,{"disambiguationData":[OSD([sQuery(id+"F0.wireOp",EDGE,"E47.MirrorCS"),sQuery(id+"F0.wireOp",EDGE,"E76.MirrorCS")])]});
            var Q15;
            Q15=makeQuery(id+"F4.opRevolve","SWEPT_EDGE",EDGE,{"disambiguationData":[OSD([sQuery(id+"F0.wireOp",EDGE,"E46.MirrorCS"),sQuery(id+"F0.wireOp",EDGE,"E75.MirrorCS")])]});
            var Q16;
            Q16=makeQuery(id+"F3.opRevolve","SWEPT_EDGE",EDGE,{"disambiguationData":[OSD([sQuery(id+"F0.wireOp",EDGE,"E18"),sQuery(id+"F0.wireOp",EDGE,"E19")])]});
            var Q17;
            Q17=makeQuery(id+"F3.opRevolve","SWEPT_EDGE",EDGE,{"disambiguationData":[OSD([sQuery(id+"F0.wireOp",EDGE,"E17"),sQuery(id+"F0.wireOp",EDGE,"E18")])]});
            var Q18;
            Q18=makeQuery(id+"F4.opRevolve","SWEPT_EDGE",EDGE,{"disambiguationData":[OSD([sQuery(id+"F0.wireOp",EDGE,"E68.MirrorCS"),sQuery(id+"F0.wireOp",EDGE,"E75.MirrorCS")])]});
            var Q19;
            Q19=makeQuery(id+"F4.opRevolve","SWEPT_EDGE",EDGE,{"disambiguationData":[OSD([sQuery(id+"F0.wireOp",EDGE,"E50.MirrorCS"),sQuery(id+"F0.wireOp",EDGE,"E69.MirrorCS")])]});
            var Q20;
            Q20=makeQuery(id+"F3.opRevolve","SWEPT_EDGE",EDGE,{"disambiguationData":[OSD([sQuery(id+"F0.wireOp",EDGE,"E20"),sQuery(id+"F0.wireOp",EDGE,"E21")])]});
            fillet(context, id + "F15", {"entities" : qUnion([Q0, Q1, Q2, Q3, Q4, Q5, Q6, Q7, Q8, Q9, Q10, Q11, Q12, Q13, Q14, Q15, Q16, Q17, Q18, Q19, Q20]), "radius" : 0.5 * mm, "tangentPropagation" : true, "allowEdgeOverflow" : false});
        }
        {
            var Q0;
            {var subQ0=sQuery(id+"F6.wireOp",EDGE,"E89");Q0=makeQuery(id+"F8.opPattern","COPY",EDGE,{"derivedFrom":makeQuery(id+"F7.opExtrude","CAP_EDGE",EDGE,{"disambiguationData":[OSD([subQ0]),TDD([makeQuery(id+"F6.imprint","IMPRINT",EDGE,{"disambiguationData":[TD([[makeQuery(id+"F6.imprint","INTERSECT",VERTEX,{"disambiguationData":[OD(1.0)],"derivedFrom":[sQuery(id+"F6.wireOp",EDGE,"E88"),subQ0]}),-1.0]])],"derivedFrom":subQ0})])],"isStart":false}),"instanceName":"1"});}
            var Q1;
            {var subQ0=sQuery(id+"F6.wireOp",EDGE,"E89");var subQ1=sQuery(id+"F6.wireOp",EDGE,"E88");var subQ4=sQuery(id+"F0.wireOp",EDGE,"E6");var subQ5=sQuery(id+"F0.wireOp",EDGE,"E5");Q1=makeQuery(id+"F10.opBoolean","SPLIT",EDGE,{"disambiguationData":[TD([makeQuery(id+"F7.opExtrude","SWEPT_FACE",FACE,{"disambiguationData":[OSD([subQ0]),TDD([makeQuery(id+"F6.imprint","IMPRINT",EDGE,{"disambiguationData":[TD([[makeQuery(id+"F6.imprint","INTERSECT",VERTEX,{"disambiguationData":[OD(0.0)],"derivedFrom":[subQ1,subQ0]}),1.0]])],"derivedFrom":subQ0})])]})])],"derivedFrom":makeQuery(id+"F9.opRevolve","SWEPT_EDGE",EDGE,{"disambiguationData":[OSD([subQ5,subQ4,sQuery(id+"F0.wireOp",EDGE,"E15")])]})});}
            var Q2;
            Q2=makeQuery(id+"F8.opPattern","COPY",EDGE,{"derivedFrom":makeQuery(id+"F7.opExtrude","CAP_EDGE",EDGE,{"disambiguationData":[OSD([sQuery(id+"F6.wireOp",EDGE,"E88")])],"isStart":false}),"instanceName":"1"});
            var Q3;
            {var subQ0=sQuery(id+"F6.wireOp",EDGE,"E89");Q3=makeQuery(id+"F8.opPattern","COPY",EDGE,{"derivedFrom":makeQuery(id+"F7.opExtrude","CAP_EDGE",EDGE,{"disambiguationData":[OSD([subQ0]),TDD([makeQuery(id+"F6.imprint","IMPRINT",EDGE,{"disambiguationData":[TD([[makeQuery(id+"F6.imprint","INTERSECT",VERTEX,{"disambiguationData":[OD(0.0)],"derivedFrom":[sQuery(id+"F6.wireOp",EDGE,"E88"),subQ0]}),1.0]])],"derivedFrom":subQ0})])],"isStart":false}),"instanceName":"1"});}
            var Q4;
            {var subQ1=sQuery(id+"F6.wireOp",EDGE,"E89");var subQ2=sQuery(id+"F6.wireOp",EDGE,"E88");var subQ4=sQuery(id+"F0.wireOp",EDGE,"E5");var subQ5=sQuery(id+"F0.wireOp",EDGE,"E6");Q4=makeQuery(id+"F10.opBoolean","SPLIT",EDGE,{"disambiguationData":[TD([makeQuery(id+"F8.opPattern","COPY",FACE,{"derivedFrom":makeQuery(id+"F7.opExtrude","SWEPT_FACE",FACE,{"disambiguationData":[OSD([subQ1]),TDD([makeQuery(id+"F6.imprint","IMPRINT",EDGE,{"disambiguationData":[TD([[makeQuery(id+"F6.imprint","INTERSECT",VERTEX,{"disambiguationData":[OD(0.0)],"derivedFrom":[subQ2,subQ1]}),1.0]])],"derivedFrom":subQ1})])]}),"instanceName":"1"})])],"derivedFrom":makeQuery(id+"F9.opRevolve","SWEPT_EDGE",EDGE,{"disambiguationData":[OSD([subQ4,subQ5,sQuery(id+"F0.wireOp",EDGE,"E15")])]})});}
            var Q5;
            {var subQ0=sQuery(id+"F6.wireOp",EDGE,"E89");Q5=makeQuery(id+"F8.opPattern","COPY",EDGE,{"derivedFrom":makeQuery(id+"F7.opExtrude","CAP_EDGE",EDGE,{"disambiguationData":[OSD([subQ0]),TDD([makeQuery(id+"F6.imprint","IMPRINT",EDGE,{"disambiguationData":[TD([[makeQuery(id+"F6.imprint","INTERSECT",VERTEX,{"disambiguationData":[OD(1.0)],"derivedFrom":[sQuery(id+"F6.wireOp",EDGE,"E88"),subQ0]}),-1.0]])],"derivedFrom":subQ0})])],"isStart":false}),"instanceName":"2"});}
            var Q6;
            Q6=makeQuery(id+"F8.opPattern","COPY",EDGE,{"derivedFrom":makeQuery(id+"F7.opExtrude","CAP_EDGE",EDGE,{"disambiguationData":[OSD([sQuery(id+"F6.wireOp",EDGE,"E88")])],"isStart":false}),"instanceName":"2"});
            var Q7;
            {var subQ0=sQuery(id+"F6.wireOp",EDGE,"E89");Q7=makeQuery(id+"F8.opPattern","COPY",EDGE,{"derivedFrom":makeQuery(id+"F7.opExtrude","CAP_EDGE",EDGE,{"disambiguationData":[OSD([subQ0]),TDD([makeQuery(id+"F6.imprint","IMPRINT",EDGE,{"disambiguationData":[TD([[makeQuery(id+"F6.imprint","INTERSECT",VERTEX,{"disambiguationData":[OD(0.0)],"derivedFrom":[sQuery(id+"F6.wireOp",EDGE,"E88"),subQ0]}),1.0]])],"derivedFrom":subQ0})])],"isStart":false}),"instanceName":"2"});}
            var Q8;
            {var subQ0=sQuery(id+"F6.wireOp",EDGE,"E89");Q8=makeQuery(id+"F7.opExtrude","CAP_EDGE",EDGE,{"disambiguationData":[OSD([subQ0]),TDD([makeQuery(id+"F6.imprint","IMPRINT",EDGE,{"disambiguationData":[TD([[makeQuery(id+"F6.imprint","INTERSECT",VERTEX,{"disambiguationData":[OD(1.0)],"derivedFrom":[sQuery(id+"F6.wireOp",EDGE,"E88"),subQ0]}),-1.0]])],"derivedFrom":subQ0})])],"isStart":false});}
            var Q9;
            Q9=makeQuery(id+"F7.opExtrude","CAP_EDGE",EDGE,{"disambiguationData":[OSD([sQuery(id+"F6.wireOp",EDGE,"E88")])],"isStart":false});
            var Q10;
            {var subQ0=sQuery(id+"F6.wireOp",EDGE,"E89");Q10=makeQuery(id+"F7.opExtrude","CAP_EDGE",EDGE,{"disambiguationData":[OSD([subQ0]),TDD([makeQuery(id+"F6.imprint","IMPRINT",EDGE,{"disambiguationData":[TD([[makeQuery(id+"F6.imprint","INTERSECT",VERTEX,{"disambiguationData":[OD(0.0)],"derivedFrom":[sQuery(id+"F6.wireOp",EDGE,"E88"),subQ0]}),1.0]])],"derivedFrom":subQ0})])],"isStart":false});}
            var Q11;
            {var subQ0=sQuery(id+"F6.wireOp",EDGE,"E89");Q11=makeQuery(id+"F7.opExtrude","CAP_EDGE",EDGE,{"disambiguationData":[OSD([subQ0]),TDD([makeQuery(id+"F6.imprint","IMPRINT",EDGE,{"disambiguationData":[TD([[makeQuery(id+"F6.imprint","INTERSECT",VERTEX,{"disambiguationData":[OD(0.0)],"derivedFrom":[sQuery(id+"F6.wireOp",EDGE,"E88"),subQ0]}),1.0]])],"derivedFrom":subQ0})])],"isStart":true});}
            var Q12;
            Q12=makeQuery(id+"F7.opExtrude","CAP_EDGE",EDGE,{"disambiguationData":[OSD([sQuery(id+"F6.wireOp",EDGE,"E88")])],"isStart":true});
            var Q13;
            {var subQ0=sQuery(id+"F6.wireOp",EDGE,"E89");Q13=makeQuery(id+"F8.opPattern","COPY",EDGE,{"derivedFrom":makeQuery(id+"F7.opExtrude","CAP_EDGE",EDGE,{"disambiguationData":[OSD([subQ0]),TDD([makeQuery(id+"F6.imprint","IMPRINT",EDGE,{"disambiguationData":[TD([[makeQuery(id+"F6.imprint","INTERSECT",VERTEX,{"disambiguationData":[OD(0.0)],"derivedFrom":[sQuery(id+"F6.wireOp",EDGE,"E88"),subQ0]}),1.0]])],"derivedFrom":subQ0})])],"isStart":true}),"instanceName":"2"});}
            var Q14;
            Q14=makeQuery(id+"F8.opPattern","COPY",EDGE,{"derivedFrom":makeQuery(id+"F7.opExtrude","CAP_EDGE",EDGE,{"disambiguationData":[OSD([sQuery(id+"F6.wireOp",EDGE,"E88")])],"isStart":true}),"instanceName":"2"});
            var Q15;
            {var subQ0=sQuery(id+"F6.wireOp",EDGE,"E89");Q15=makeQuery(id+"F8.opPattern","COPY",EDGE,{"derivedFrom":makeQuery(id+"F7.opExtrude","CAP_EDGE",EDGE,{"disambiguationData":[OSD([subQ0]),TDD([makeQuery(id+"F6.imprint","IMPRINT",EDGE,{"disambiguationData":[TD([[makeQuery(id+"F6.imprint","INTERSECT",VERTEX,{"disambiguationData":[OD(1.0)],"derivedFrom":[sQuery(id+"F6.wireOp",EDGE,"E88"),subQ0]}),-1.0]])],"derivedFrom":subQ0})])],"isStart":true}),"instanceName":"2"});}
            var Q16;
            {var subQ1=sQuery(id+"F6.wireOp",EDGE,"E89");var subQ2=sQuery(id+"F6.wireOp",EDGE,"E88");var subQ4=sQuery(id+"F0.wireOp",EDGE,"E59.MirrorCS");var subQ5=sQuery(id+"F0.wireOp",EDGE,"E80.MirrorCS");Q16=makeQuery(id+"F10.opBoolean","SPLIT",EDGE,{"disambiguationData":[TD([makeQuery(id+"F8.opPattern","COPY",FACE,{"derivedFrom":makeQuery(id+"F7.opExtrude","SWEPT_FACE",FACE,{"disambiguationData":[OSD([subQ1]),TDD([makeQuery(id+"F6.imprint","IMPRINT",EDGE,{"disambiguationData":[TD([[makeQuery(id+"F6.imprint","INTERSECT",VERTEX,{"disambiguationData":[OD(0.0)],"derivedFrom":[subQ2,subQ1]}),1.0]])],"derivedFrom":subQ1})])]}),"instanceName":"1"})])],"derivedFrom":makeQuery(id+"F9.opRevolve","SWEPT_EDGE",EDGE,{"disambiguationData":[OSD([subQ4,sQuery(id+"F0.wireOp",EDGE,"E73.MirrorCS"),subQ5])]})});}
            var Q17;
            {var subQ0=sQuery(id+"F6.wireOp",EDGE,"E89");Q17=makeQuery(id+"F8.opPattern","COPY",EDGE,{"derivedFrom":makeQuery(id+"F7.opExtrude","CAP_EDGE",EDGE,{"disambiguationData":[OSD([subQ0]),TDD([makeQuery(id+"F6.imprint","IMPRINT",EDGE,{"disambiguationData":[TD([[makeQuery(id+"F6.imprint","INTERSECT",VERTEX,{"disambiguationData":[OD(0.0)],"derivedFrom":[sQuery(id+"F6.wireOp",EDGE,"E88"),subQ0]}),1.0]])],"derivedFrom":subQ0})])],"isStart":true}),"instanceName":"1"});}
            var Q18;
            Q18=makeQuery(id+"F8.opPattern","COPY",EDGE,{"derivedFrom":makeQuery(id+"F7.opExtrude","CAP_EDGE",EDGE,{"disambiguationData":[OSD([sQuery(id+"F6.wireOp",EDGE,"E88")])],"isStart":true}),"instanceName":"1"});
            var Q19;
            {var subQ0=sQuery(id+"F6.wireOp",EDGE,"E89");Q19=makeQuery(id+"F8.opPattern","COPY",EDGE,{"derivedFrom":makeQuery(id+"F7.opExtrude","CAP_EDGE",EDGE,{"disambiguationData":[OSD([subQ0]),TDD([makeQuery(id+"F6.imprint","IMPRINT",EDGE,{"disambiguationData":[TD([[makeQuery(id+"F6.imprint","INTERSECT",VERTEX,{"disambiguationData":[OD(1.0)],"derivedFrom":[sQuery(id+"F6.wireOp",EDGE,"E88"),subQ0]}),-1.0]])],"derivedFrom":subQ0})])],"isStart":true}),"instanceName":"1"});}
            var Q20;
            {var subQ0=sQuery(id+"F6.wireOp",EDGE,"E89");var subQ1=sQuery(id+"F6.wireOp",EDGE,"E88");var subQ4=sQuery(id+"F0.wireOp",EDGE,"E59.MirrorCS");var subQ5=sQuery(id+"F0.wireOp",EDGE,"E80.MirrorCS");Q20=makeQuery(id+"F10.opBoolean","SPLIT",EDGE,{"disambiguationData":[TD([makeQuery(id+"F7.opExtrude","SWEPT_FACE",FACE,{"disambiguationData":[OSD([subQ0]),TDD([makeQuery(id+"F6.imprint","IMPRINT",EDGE,{"disambiguationData":[TD([[makeQuery(id+"F6.imprint","INTERSECT",VERTEX,{"disambiguationData":[OD(0.0)],"derivedFrom":[subQ1,subQ0]}),1.0]])],"derivedFrom":subQ0})])]})])],"derivedFrom":makeQuery(id+"F9.opRevolve","SWEPT_EDGE",EDGE,{"disambiguationData":[OSD([subQ4,sQuery(id+"F0.wireOp",EDGE,"E73.MirrorCS"),subQ5])]})});}
            var Q21;
            {var subQ0=sQuery(id+"F6.wireOp",EDGE,"E89");Q21=makeQuery(id+"F7.opExtrude","CAP_EDGE",EDGE,{"disambiguationData":[OSD([subQ0]),TDD([makeQuery(id+"F6.imprint","IMPRINT",EDGE,{"disambiguationData":[TD([[makeQuery(id+"F6.imprint","INTERSECT",VERTEX,{"disambiguationData":[OD(1.0)],"derivedFrom":[sQuery(id+"F6.wireOp",EDGE,"E88"),subQ0]}),-1.0]])],"derivedFrom":subQ0})])],"isStart":true});}
            var Q22;
            {var subQ1=sQuery(id+"F6.wireOp",EDGE,"E89");var subQ2=sQuery(id+"F6.wireOp",EDGE,"E88");var subQ4=sQuery(id+"F0.wireOp",EDGE,"E59.MirrorCS");var subQ5=sQuery(id+"F0.wireOp",EDGE,"E80.MirrorCS");Q22=makeQuery(id+"F10.opBoolean","SPLIT",EDGE,{"disambiguationData":[TD([makeQuery(id+"F7.opExtrude","SWEPT_FACE",FACE,{"disambiguationData":[OSD([subQ1]),TDD([makeQuery(id+"F6.imprint","IMPRINT",EDGE,{"disambiguationData":[TD([[makeQuery(id+"F6.imprint","INTERSECT",VERTEX,{"disambiguationData":[OD(1.0)],"derivedFrom":[subQ2,subQ1]}),-1.0]])],"derivedFrom":subQ1})])]})])],"derivedFrom":makeQuery(id+"F9.opRevolve","SWEPT_EDGE",EDGE,{"disambiguationData":[OSD([subQ4,sQuery(id+"F0.wireOp",EDGE,"E73.MirrorCS"),subQ5])]})});}
            var Q23;
            {var subQ1=sQuery(id+"F6.wireOp",EDGE,"E89");var subQ2=sQuery(id+"F6.wireOp",EDGE,"E88");var subQ4=sQuery(id+"F0.wireOp",EDGE,"E5");var subQ5=sQuery(id+"F0.wireOp",EDGE,"E6");Q23=makeQuery(id+"F10.opBoolean","SPLIT",EDGE,{"disambiguationData":[TD([makeQuery(id+"F7.opExtrude","SWEPT_FACE",FACE,{"disambiguationData":[OSD([subQ1]),TDD([makeQuery(id+"F6.imprint","IMPRINT",EDGE,{"disambiguationData":[TD([[makeQuery(id+"F6.imprint","INTERSECT",VERTEX,{"disambiguationData":[OD(1.0)],"derivedFrom":[subQ2,subQ1]}),-1.0]])],"derivedFrom":subQ1})])]})])],"derivedFrom":makeQuery(id+"F9.opRevolve","SWEPT_EDGE",EDGE,{"disambiguationData":[OSD([subQ4,subQ5,sQuery(id+"F0.wireOp",EDGE,"E15")])]})});}
            chamfer(context, id + "F16", {"entities" : qUnion([Q0, Q1, Q2, Q3, Q4, Q5, Q6, Q7, Q8, Q9, Q10, Q11, Q12, Q13, Q14, Q15, Q16, Q17, Q18, Q19, Q20, Q21, Q22, Q23]), "width" : 1.5 * mm, "tangentPropagation" : true});
        }
    });
